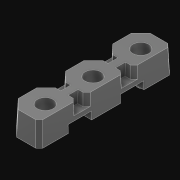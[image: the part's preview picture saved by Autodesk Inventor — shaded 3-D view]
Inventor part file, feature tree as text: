
AUTODESK INVENTOR PART (.ipt)
format: ipt  version: 2021 (Build 250183000, 183)  size: 331,776 bytes
history: native  units: in
note: dims shown in document units (in); Inventor stores cm internally (conversion verified against a paired STEP export)
features: other x9, sketch x1
ambient origin geometry x8: Origin, YZ Plane, XZ Plane, XY Plane, X Axis, Y Axis, Z Axis, Center Point
bodies: Solid1 (feature_tree)
feature tree (10):
  other  "Bearing Flat - Cut.ipt"
  other  "NONE::Bearing Flat - Cut.ipt"
  other  "TaggingFeature1"
  sketch  "Sketch1"  dims[d0=0.3937in]
  other  "Srf1"
  other  "Srf2"
  other  "Srf3"
  other  "Srf1::Derived"
  other  "Srf2::Derived"
  other  "Srf3::Derived"
